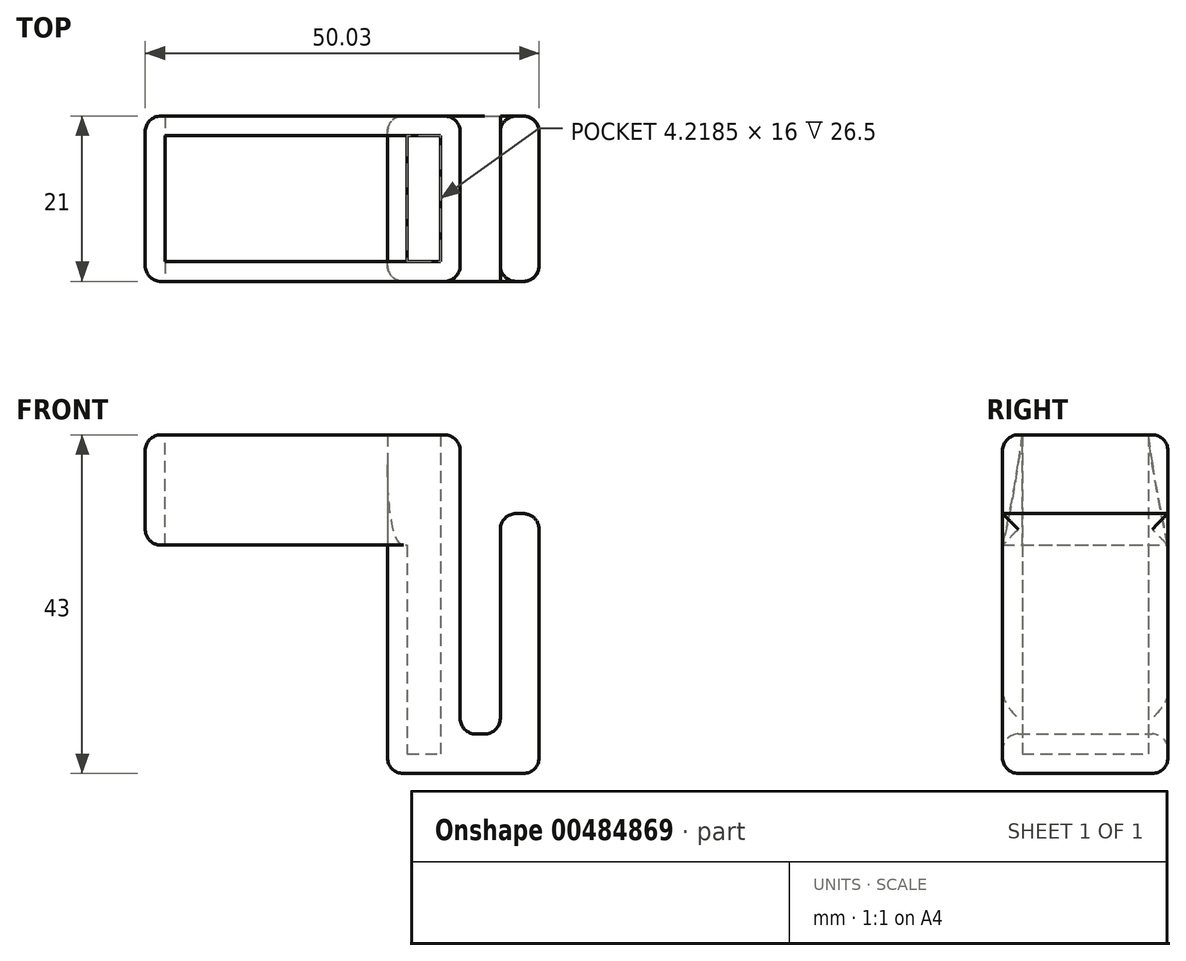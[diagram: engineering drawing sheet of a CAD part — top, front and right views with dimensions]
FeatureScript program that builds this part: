
annotation { "Feature Type Name" : "Feature", "Feature Type Description" : "" }
export const myFeature = defineFeature(function(context is Context, id is Id, definition is map)
    precondition{}
    {
        {
            var Q0;
            Q0=qCreatedBy(makeId("Front.planeOp"),FACE);
            var sketch = newSketch(context, id + "F0", { "sketchPlane" : qUnion([Q0])});
            skLineSegment(sketch, "E0", {"start": v(-50.03, 38) * mm, "end": v(-50.03, 24) * mm});
            skLineSegment(sketch, "E1", {"start": v(-50.03, 24) * mm, "end": v(-19.25, 24) * mm});
            skLineSegment(sketch, "E2", {"start": v(-50.03, 38) * mm, "end": v(-10.03, 38) * mm});
            skLineSegment(sketch, "E3", {"start": v(-10.03, 38) * mm, "end": v(-10.03, 0) * mm});
            skLineSegment(sketch, "E4", {"start": v(-10.03, -5) * mm, "end": v(0, -5) * mm});
            skLineSegment(sketch, "E5", {"start": v(0, -5) * mm, "end": v(0, 28) * mm});
            skLineSegment(sketch, "E6", {"start": v(0, 28) * mm, "end": v(-4.93, 28) * mm});
            skLineSegment(sketch, "E7", {"start": v(-4.93, 28) * mm, "end": v(-4.93, 0) * mm});
            skLineSegment(sketch, "E8", {"start": v(-10.03, 0) * mm, "end": v(-4.93, 0) * mm});
            skLineSegment(sketch, "E9", {"start": v(-19.25, 24) * mm, "end": v(-19.25, -5) * mm});
            skLineSegment(sketch, "E10", {"start": v(-19.25, -5) * mm, "end": v(-10.03, -5) * mm});
            skSolve(sketch);
        }
        {
            var Q0;
            Q0 = qSketchRegion(id + "F0", true);
            extrude(context, id + "F1", {"entities" : qUnion([Q0]), "depth" : 21 * mm});
        }
        {
            var Q0;
            Q0=makeQuery(id+"F1.opExtrude","SWEPT_FACE",FACE,{"disambiguationData":[OSD([sQuery(id+"F0.wireOp",EDGE,"E2")])]});
            var Q1;
            Q1=makeQuery(id+"F1.opExtrude","SWEPT_FACE",FACE,{"disambiguationData":[OSD([sQuery(id+"F0.wireOp",EDGE,"E1")])]});
            shell(context, id + "F2", {"entities" : qUnion([Q0, Q1]), "thickness" : 2.5 * mm});
        }
        {
            var Q0;
            Q0=makeQuery(id+"F1.opExtrude","SWEPT_EDGE",EDGE,{"disambiguationData":[OSD([sQuery(id+"F0.wireOp",EDGE,"E6"),sQuery(id+"F0.wireOp",EDGE,"E7")])]});
            var Q1;
            Q1=makeQuery(id+"F1.opExtrude","SWEPT_EDGE",EDGE,{"disambiguationData":[OSD([sQuery(id+"F0.wireOp",EDGE,"E7"),sQuery(id+"F0.wireOp",EDGE,"E8")])]});
            var Q2;
            Q2=makeQuery(id+"F1.opExtrude","CAP_EDGE",EDGE,{"disambiguationData":[OSD([sQuery(id+"F0.wireOp",EDGE,"E8")])],"isStart":true});
            var Q3;
            Q3=makeQuery(id+"F1.opExtrude","CAP_EDGE",EDGE,{"disambiguationData":[OSD([sQuery(id+"F0.wireOp",EDGE,"E8")])],"isStart":false});
            var Q4;
            Q4=makeQuery(id+"F1.opExtrude","CAP_EDGE",EDGE,{"disambiguationData":[OSD([sQuery(id+"F0.wireOp",EDGE,"E3")])],"isStart":false});
            var Q5;
            Q5=makeQuery(id+"F1.opExtrude","CAP_EDGE",EDGE,{"disambiguationData":[OSD([sQuery(id+"F0.wireOp",EDGE,"E3")])],"isStart":true});
            var Q6;
            Q6=makeQuery(id+"F1.opExtrude","CAP_EDGE",EDGE,{"disambiguationData":[OSD([sQuery(id+"F0.wireOp",EDGE,"E5")])],"isStart":false});
            var Q7;
            Q7=makeQuery(id+"F1.opExtrude","SWEPT_EDGE",EDGE,{"disambiguationData":[OSD([sQuery(id+"F0.wireOp",EDGE,"E5"),sQuery(id+"F0.wireOp",EDGE,"E6")])]});
            var Q8;
            Q8=makeQuery(id+"F1.opExtrude","CAP_EDGE",EDGE,{"disambiguationData":[OSD([sQuery(id+"F0.wireOp",EDGE,"E5")])],"isStart":true});
            var Q9;
            Q9=makeQuery(id+"F1.opExtrude","SWEPT_EDGE",EDGE,{"disambiguationData":[OSD([sQuery(id+"F0.wireOp",EDGE,"E4"),sQuery(id+"F0.wireOp",EDGE,"E5")])]});
            var Q10;
            Q10=makeQuery(id+"F1.opExtrude","CAP_EDGE",EDGE,{"disambiguationData":[OSD([sQuery(id+"F0.wireOp",EDGE,"E4"),sQuery(id+"F0.wireOp",EDGE,"E10")])],"isStart":false});
            var Q11;
            Q11=makeQuery(id+"F1.opExtrude","CAP_EDGE",EDGE,{"disambiguationData":[OSD([sQuery(id+"F0.wireOp",EDGE,"E9")])],"isStart":false});
            var Q12;
            Q12=makeQuery(id+"F1.opExtrude","CAP_EDGE",EDGE,{"disambiguationData":[OSD([sQuery(id+"F0.wireOp",EDGE,"E0")])],"isStart":false});
            var Q13;
            Q13=makeQuery(id+"F1.opExtrude","SWEPT_EDGE",EDGE,{"disambiguationData":[OSD([sQuery(id+"F0.wireOp",EDGE,"E0"),sQuery(id+"F0.wireOp",EDGE,"E1")])]});
            var Q14;
            Q14=makeQuery(id+"F1.opExtrude","CAP_EDGE",EDGE,{"disambiguationData":[OSD([sQuery(id+"F0.wireOp",EDGE,"E0")])],"isStart":true});
            var Q15;
            Q15=makeQuery(id+"F1.opExtrude","SWEPT_EDGE",EDGE,{"disambiguationData":[OSD([sQuery(id+"F0.wireOp",EDGE,"E0"),sQuery(id+"F0.wireOp",EDGE,"E2")])]});
            var Q16;
            Q16=makeQuery(id+"F1.opExtrude","CAP_EDGE",EDGE,{"disambiguationData":[OSD([sQuery(id+"F0.wireOp",EDGE,"E9")])],"isStart":true});
            var Q17;
            Q17=makeQuery(id+"F1.opExtrude","SWEPT_EDGE",EDGE,{"disambiguationData":[OSD([sQuery(id+"F0.wireOp",EDGE,"E9"),sQuery(id+"F0.wireOp",EDGE,"E10")])]});
            var Q18;
            Q18=makeQuery(id+"F1.opExtrude","CAP_EDGE",EDGE,{"disambiguationData":[OSD([sQuery(id+"F0.wireOp",EDGE,"E4"),sQuery(id+"F0.wireOp",EDGE,"E10")])],"isStart":true});
            var Q19;
            Q19=makeQuery(id+"F1.opExtrude","CAP_EDGE",EDGE,{"disambiguationData":[OSD([sQuery(id+"F0.wireOp",EDGE,"E2")])],"isStart":true});
            var Q20;
            Q20=makeQuery(id+"F1.opExtrude","CAP_EDGE",EDGE,{"disambiguationData":[OSD([sQuery(id+"F0.wireOp",EDGE,"E2")])],"isStart":false});
            var Q21;
            Q21=makeQuery(id+"F1.opExtrude","SWEPT_EDGE",EDGE,{"disambiguationData":[OSD([sQuery(id+"F0.wireOp",EDGE,"E2"),sQuery(id+"F0.wireOp",EDGE,"E3")])]});
            var Q22;
            Q22=makeQuery(id+"F1.opExtrude","SWEPT_EDGE",EDGE,{"disambiguationData":[OSD([sQuery(id+"F0.wireOp",EDGE,"E3"),sQuery(id+"F0.wireOp",EDGE,"E8")])]});
            fillet(context, id + "F3", {"entities" : qUnion([Q0, Q1, Q2, Q3, Q4, Q5, Q6, Q7, Q8, Q9, Q10, Q11, Q12, Q13, Q14, Q15, Q16, Q17, Q18, Q19, Q20, Q21, Q22]), "radius" : 2 * mm, "tangentPropagation" : true, "allowEdgeOverflow" : false});
        }
        {
            var Q0;
            {var subQ0=sQuery(id+"F0.wireOp",EDGE,"E1");Q0=makeQuery(id+"F2.opShell","OFFSET_EDGE",EDGE,{"disambiguationData":[OSD([subQ0]),TDD([makeQuery(id+"F1.opExtrude","CAP_EDGE",EDGE,{"disambiguationData":[OSD([subQ0])],"isStart":false})]),OD(0.0)]});}
            var Q1;
            {var subQ0=sQuery(id+"F0.wireOp",EDGE,"E1");Q1=makeQuery(id+"F2.opShell","OFFSET_EDGE",EDGE,{"disambiguationData":[OSD([subQ0]),TDD([makeQuery(id+"F1.opExtrude","CAP_EDGE",EDGE,{"disambiguationData":[OSD([subQ0])],"isStart":true})]),OD(0.0)]});}
            fillet(context, id + "F4", {"entities" : qUnion([Q0, Q1]), "radius" : 120 * mm, "tangentPropagation" : true, "rho" : .4, "crossSection" : FilletCrossSection.CONIC, "allowEdgeOverflow" : false});
        }
    });
